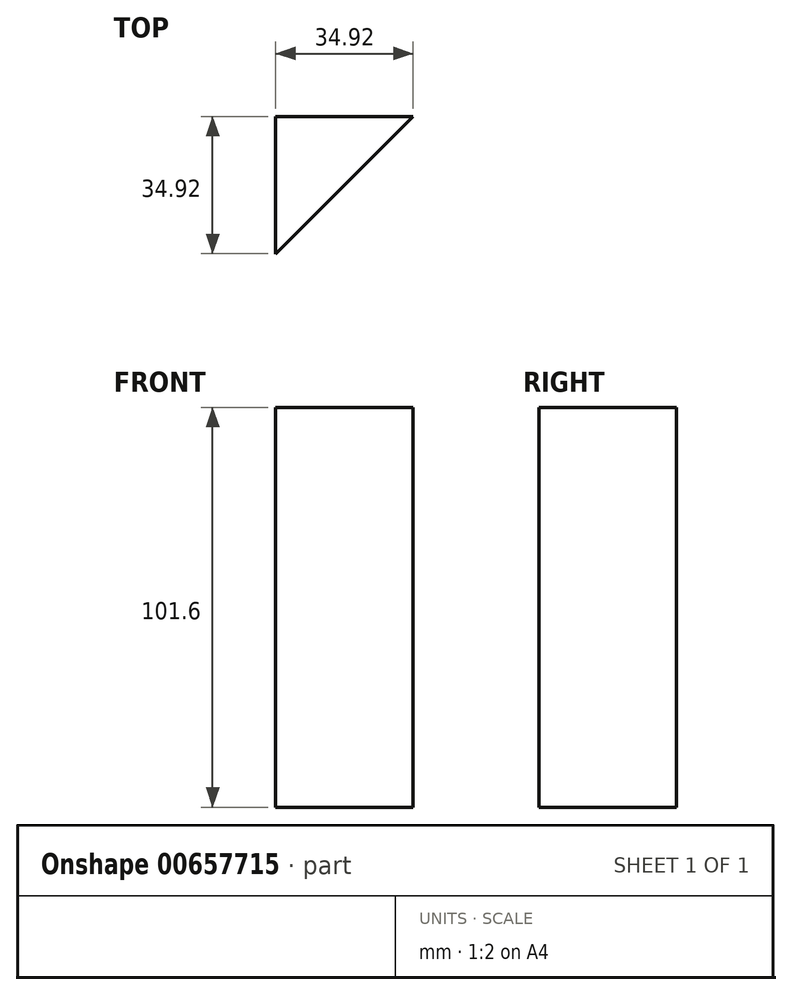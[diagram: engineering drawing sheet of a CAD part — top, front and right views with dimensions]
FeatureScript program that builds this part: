
annotation { "Feature Type Name" : "Feature", "Feature Type Description" : "" }
export const myFeature = defineFeature(function(context is Context, id is Id, definition is map)
    precondition{}
    {
        {
            var Q0;
            Q0=qCreatedBy(makeId("Top.planeOp"),FACE);
            var sketch = newSketch(context, id + "F0", { "sketchPlane" : qUnion([Q0])});
            skLineSegment(sketch, "E0", {"start": v(0, 0) * mm, "end": v(0, -34.93) * mm});
            skLineSegment(sketch, "E1", {"start": v(0, 0) * mm, "end": v(34.93, 0) * mm});
            skLineSegment(sketch, "E2", {"start": v(0, -34.92) * mm, "end": v(34.92, 0) * mm});
            skSolve(sketch);
        }
        {
            var Q0;
            Q0=makeQuery(id+"F0.imprint","IMPRINT",FACE,{"disambiguationData":[TD([[makeQuery(id+"F0.imprint","IMPRINT",EDGE,{"derivedFrom":sQuery(id+"F0.wireOp",EDGE,"E0")}),1.0]])]});
            extrude(context, id + "F1", {"entities" : qUnion([Q0]), "depth" : 101.6 * mm, "offsetDistance" : 25.4 * mm});
        }
    });
